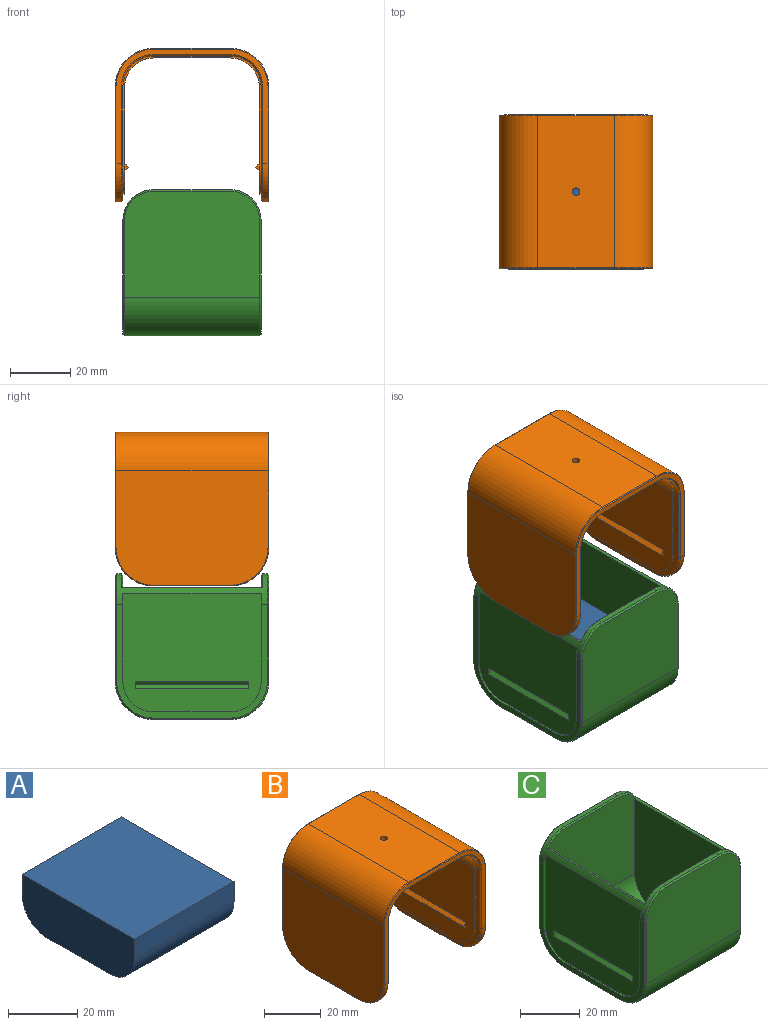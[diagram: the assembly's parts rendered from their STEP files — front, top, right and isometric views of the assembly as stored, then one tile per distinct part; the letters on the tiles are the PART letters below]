
ASSEMBLY  parts=3 mates=1
PART A: 8 faces, bbox 40.6x45.7x17.3 mm
  f0: plane 40.64x7.1mm, normal (0,1,0), area 288.6mm2, adj f1,f5,f6,f7
  f1: plane 45.72x40.64mm, normal (0,0,1), area 1858.1mm2, adj f0,f2,f6,f7
  f2: plane 40.64x7.1mm, normal (0,-1,0), area 288.6mm2, adj f1,f3,f6,f7
  f3: cylinder r=10.16mm len=40.64mm, axis (-1,0,0), area 648.6mm2, adj f2,f4,f6,f7
  f4: plane 40.64x25.4mm, normal (0,0,-1), area 1032.3mm2, adj f3,f5,f6,f7
  f5: cylinder r=10.16mm len=40.64mm, axis (-1,0,0), area 648.6mm2, adj f0,f4,f6,f7
  f6: plane 45.72x17.26mm, normal (1,0,0), area 744.9mm2, adj f0,f1,f2,f3,f4,f5
  f7: plane 45.72x17.26mm, normal (-1,0,0), area 744.9mm2, adj f0,f1,f2,f3,f4,f5
PART B: 75 faces, bbox 50.8x50.8x50.8 mm
  f0: plane 25.4x2.03mm, normal (0,0,-1), area 51.6mm2, adj f2,f12,f22,f43
  f1: cylinder r=10.16mm len=10.16mm, axis (0,1,0), area 32.4mm2, adj f3,f13,f21,f54
  f2: cylinder r=10.16mm len=10.16mm, axis (0,1,0), area 32.4mm2, adj f0,f4,f22,f45
  f3: plane 49.78x37.59mm, normal (1,0,0), area 226.2mm2, adj f1,f12,f21,f22,f29,f30,f31,f44
  f4: plane 49.78x37.59mm, normal (-1,0,0), area 226.2mm2, adj f2,f14,f21,f22,f23,f24,f25,f47
  f5: plane 25.4x1.78mm, normal (0,0,-1), area 45.2mm2, adj f18,f20,f51,f66
  f6: plane 50.29x37.85mm, normal (1,0,0), area 1836.9mm2, adj f7,f62,f64,f66,f68,f70
  f7: cylinder r=12.7mm len=50.29mm, axis (0,1,0), area 1003.3mm2, adj f6,f8,f60,f72
  f8: plane 50.29x25.4mm, normal (0,0,1), area 1272.3mm2, adj f7,f9,f58,f73,f74
  f9: cylinder r=12.7mm len=50.29mm, axis (0,1,0), area 1003.3mm2, adj f8,f10,f59,f71
  f10: plane 50.29x37.85mm, normal (-1,0,0), area 1836.9mm2, adj f9,f61,f63,f65,f67,f69
  f11: plane 25.4x1.78mm, normal (0,0,-1), area 45.2mm2, adj f17,f19,f48,f65
  f12: cylinder r=10.16mm len=10.16mm, axis (0,1,0), area 32.4mm2, adj f0,f3,f22,f42
  f13: plane 25.4x2.03mm, normal (0,0,-1), area 51.6mm2, adj f1,f14,f21,f56
  f14: cylinder r=10.16mm len=10.16mm, axis (0,1,0), area 32.4mm2, adj f4,f13,f21,f57
  f15: plane 50.29x37.85mm, normal (0,-1,0), area 200mm2, adj f19,f20,f42,f43,f44,f45,f47,f58
  f16: plane 50.29x37.85mm, normal (0,1,0), area 200mm2, adj f17,f18,f52,f54,f55,f56,f57,f69
  f17: cylinder r=12.7mm len=12.7mm, axis (1,0,0), area 35.5mm2, adj f11,f16,f50,f67
  f18: cylinder r=12.7mm len=12.7mm, axis (1,0,0), area 35.5mm2, adj f5,f16,f53,f68
  f19: cylinder r=12.7mm len=12.7mm, axis (-1,0,0), area 35.5mm2, adj f11,f15,f46,f63
  f20: cylinder r=12.7mm len=12.7mm, axis (-1,0,0), area 35.5mm2, adj f5,f15,f49,f64
  f21: plane 45.72x35.56mm, normal (0,1,0), area 68mm2, adj f1,f3,f4,f13,f14,f25,f26,f31
  f22: plane 45.72x35.56mm, normal (0,-1,0), area 68mm2, adj f0,f2,f3,f4,f12,f23,f26,f29
  f23: cylinder r=10.16mm len=10.16mm, axis (1,0,0), area 10.1mm2, adj f4,f22,f24,f26
  f24: plane 25.4x0.64mm, normal (0,0,-1), area 16.1mm2, adj f4,f23,f25,f26
  f25: cylinder r=10.16mm len=10.16mm, axis (1,0,0), area 10.1mm2, adj f4,f21,f24,f26
  f26: plane 45.72x35.56mm, normal (-1,0,0), area 1489.5mm2, adj f21,f22,f23,f24,f25,f27,f28,f35
  f27: plane 2.46x1.23mm, normal (0,-1,0), area 1.5mm2, adj f26,f35,f36
  f28: plane 2.46x1.23mm, normal (0,1,0), area 1.5mm2, adj f26,f35,f36
  f29: cylinder r=10.16mm len=10.16mm, axis (-1,0,0), area 10.1mm2, adj f3,f22,f30,f32
  f30: plane 25.4x0.64mm, normal (0,0,-1), area 16.1mm2, adj f3,f29,f31,f32
  f31: cylinder r=10.16mm len=10.16mm, axis (-1,0,0), area 10.1mm2, adj f3,f21,f30,f32
  f32: plane 45.72x35.56mm, normal (1,0,0), area 1489.5mm2, adj f21,f22,f29,f30,f31,f33,f34,f37
  f33: plane 2.46x1.23mm, normal (0,1,0), area 1.5mm2, adj f32,f37,f38
  f34: plane 2.46x1.23mm, normal (0,-1,0), area 1.5mm2, adj f32,f37,f38
  f35: plane 37.4x1.23mm, normal (-0.71,0,0.71), area 65.1mm2, adj f26,f27,f28,f36
  f36: plane 37.4x1.23mm, normal (-0.71,0,-0.71), area 65.1mm2, adj f26,f27,f28,f35
  f37: plane 37.4x1.23mm, normal (0.71,0,0.71), area 65.1mm2, adj f32,f33,f34,f38
  f38: plane 37.4x1.23mm, normal (0.71,0,-0.71), area 65.1mm2, adj f32,f33,f34,f37
  f39: cylinder r=9.53mm len=45.72mm, axis (0,-1,0), area 684.1mm2, adj f21,f22,f26,f41
  f40: cylinder r=9.53mm len=45.72mm, axis (0,-1,0), area 684.1mm2, adj f21,f22,f32,f41
  f41: plane 45.72x25.4mm, normal (0,0,-1), area 1156.2mm2, adj f21,f22,f39,f40,f74
  f42: cone r=10.67mm half-angle=45deg, axis (0,-1,0), area 11.8mm2, adj f12,f15,f43,f44
  f43: plane 25.4x0.51mm, normal (0,-0.71,-0.71), area 18.2mm2, adj f0,f15,f42,f45
  f44: plane 25.4x0.51mm, normal (0.71,-0.71,0), area 18.2mm2, adj f3,f15,f42,f46
  f45: cone r=10.16mm half-angle=45deg, axis (0,-1,0), area 11.8mm2, adj f2,f15,f43,f47
  f46: cone r=12.19mm half-angle=45deg, axis (-1,0,0), area 14mm2, adj f3,f19,f44,f48
  f47: plane 25.4x0.51mm, normal (-0.71,-0.71,0), area 18.2mm2, adj f4,f15,f45,f49
  f48: plane 25.4x0.51mm, normal (0.71,0,-0.71), area 18.2mm2, adj f3,f11,f46,f50
  f49: cone r=12.19mm half-angle=45deg, axis (1,0,0), area 14mm2, adj f4,f20,f47,f51
  f50: cone r=12.19mm half-angle=45deg, axis (-1,0,0), area 14mm2, adj f3,f17,f48,f52
  f51: plane 25.4x0.51mm, normal (-0.71,0,-0.71), area 18.2mm2, adj f4,f5,f49,f53
  f52: plane 25.4x0.51mm, normal (0.71,0.71,0), area 18.2mm2, adj f3,f16,f50,f54
  f53: cone r=12.19mm half-angle=45deg, axis (1,0,0), area 14mm2, adj f4,f18,f51,f55
  f54: cone r=10.16mm half-angle=45deg, axis (0,1,0), area 11.8mm2, adj f1,f16,f52,f56
  f55: plane 25.4x0.51mm, normal (-0.71,0.71,0), area 18.2mm2, adj f4,f16,f53,f57
  f56: plane 25.4x0.51mm, normal (0,0.71,-0.71), area 18.2mm2, adj f13,f16,f54,f57
  f57: cone r=10.67mm half-angle=45deg, axis (0,1,0), area 11.8mm2, adj f14,f16,f55,f56
  f58: plane 25.4x0.25mm, normal (0,-0.71,0.71), area 9.1mm2, adj f8,f15,f59,f60
  f59: cone r=12.7mm half-angle=45deg, axis (0,1,0), area 7.1mm2, adj f9,f15,f58,f61
  f60: cone r=12.45mm half-angle=45deg, axis (0,1,0), area 7.1mm2, adj f7,f15,f58,f62
  f61: plane 25.4x0.25mm, normal (-0.71,-0.71,0), area 9.1mm2, adj f10,f15,f59,f63
  f62: plane 25.4x0.25mm, normal (0.71,-0.71,0), area 9.1mm2, adj f6,f15,f60,f64
  f63: cone r=12.45mm half-angle=45deg, axis (1,0,0), area 7.1mm2, adj f10,f19,f61,f65
  f64: cone r=12.45mm half-angle=45deg, axis (-1,0,0), area 7.1mm2, adj f6,f20,f62,f66
  f65: plane 25.4x0.25mm, normal (-0.71,0,-0.71), area 9.1mm2, adj f10,f11,f63,f67
  f66: plane 25.4x0.25mm, normal (0.71,0,-0.71), area 9.1mm2, adj f5,f6,f64,f68
  f67: cone r=12.45mm half-angle=45deg, axis (1,0,0), area 7.1mm2, adj f10,f17,f65,f69
  f68: cone r=12.45mm half-angle=45deg, axis (-1,0,0), area 7.1mm2, adj f6,f18,f66,f70
  f69: plane 25.4x0.25mm, normal (-0.71,0.71,0), area 9.1mm2, adj f10,f16,f67,f71
  f70: plane 25.4x0.25mm, normal (0.71,0.71,0), area 9.1mm2, adj f6,f16,f68,f72
  f71: cone r=12.45mm half-angle=45deg, axis (0,-1,0), area 7.1mm2, adj f9,f16,f69,f73
  f72: cone r=12.7mm half-angle=45deg, axis (0,-1,0), area 7.1mm2, adj f7,f16,f70,f73
  f73: plane 25.4x0.25mm, normal (0,0.71,0.71), area 9.1mm2, adj f8,f16,f71,f72
  f74: cylinder r=1.27mm len=3.18mm, axis (0,0,1), area 25.3mm2, adj f8,f41
PART C: 62 faces, bbox 45.7x50.8x48.3 mm
  f0: plane 28.94x0.64mm, normal (0,1,0), area 17.6mm2, adj f5,f8,f28,f31
  f1: plane 41.44x35.08mm, normal (0,-1,0), area 1408.8mm2, adj f18,f19,f20,f54,f55,f56,f57,f59
  f2: plane 41.44x35.08mm, normal (0,1,0), area 1408.8mm2, adj f18,f19,f21,f56,f58,f59,f60,f61
  f3: plane 28.94x0.64mm, normal (0,-1,0), area 17.6mm2, adj f4,f10,f23,f25
  f4: plane 49.78x37.59mm, normal (-1,0,0), area 226.2mm2, adj f3,f10,f13,f22,f23,f24,f41,f43
  f5: plane 49.78x37.59mm, normal (1,0,0), area 226.2mm2, adj f0,f8,f14,f28,f29,f30,f42,f44
  f6: plane 25.4x1.55mm, normal (0,0,1), area 39.4mm2, adj f8,f10,f53,f55
  f7: plane 44.7x25.4mm, normal (0,0,-1), area 1135.5mm2, adj f15,f16,f45,f46
  f8: cylinder r=10.16mm len=49.78mm, axis (0,1,0), area 159.2mm2, adj f0,f5,f6,f9,f14,f31,f40,f52
  f9: plane 25.4x1.55mm, normal (0,0,1), area 39.4mm2, adj f8,f10,f38,f60
  f10: cylinder r=10.16mm len=49.78mm, axis (0,1,0), area 159.2mm2, adj f3,f4,f6,f9,f13,f25,f39,f51
  f11: plane 44.7x35.05mm, normal (0,-1,0), area 1527mm2, adj f16,f38,f39,f40,f41,f42
  f12: plane 44.7x35.05mm, normal (0,1,0), area 1527mm2, adj f15,f49,f50,f51,f52,f53
  f13: plane 28.94x0.64mm, normal (0,1,0), area 17.6mm2, adj f4,f10,f22,f25
  f14: plane 28.94x0.64mm, normal (0,-1,0), area 17.6mm2, adj f5,f8,f30,f31
  f15: cylinder r=12.7mm len=44.7mm, axis (1,0,0), area 891.8mm2, adj f7,f12,f47,f48
  f16: cylinder r=12.7mm len=44.7mm, axis (-1,0,0), area 891.8mm2, adj f7,f11,f43,f44
  f17: plane 40.64x25.4mm, normal (0,0,1), area 1032.3mm2, adj f18,f19,f20,f21
  f18: plane 45.72x40.86mm, normal (-1,0,0), area 1823.8mm2, adj f1,f2,f17,f20,f21,f56
  f19: plane 45.72x40.86mm, normal (1,0,0), area 1823.8mm2, adj f1,f2,f17,f20,f21,f59
  f20: cylinder r=10.16mm len=40.64mm, axis (1,0,0), area 648.6mm2, adj f1,f17,f18,f19
  f21: cylinder r=10.16mm len=40.64mm, axis (-1,0,0), area 648.6mm2, adj f2,f17,f18,f19
  f22: cylinder r=10.16mm len=10.16mm, axis (-1,0,0), area 10.1mm2, adj f4,f13,f24,f25
  f23: cylinder r=10.16mm len=10.16mm, axis (-1,0,0), area 10.1mm2, adj f3,f4,f24,f25
  f24: plane 25.4x0.64mm, normal (0,0,1), area 16.1mm2, adj f4,f22,f23,f25
  f25: plane 45.72x39.1mm, normal (-1,0,0), area 1651.1mm2, adj f3,f10,f13,f22,f23,f24,f26,f27
  f26: plane 2.46x1.23mm, normal (0,-1,0), area 1.5mm2, adj f25,f34,f35
  f27: plane 2.46x1.23mm, normal (0,1,0), area 1.5mm2, adj f25,f34,f35
  f28: cylinder r=10.16mm len=10.16mm, axis (1,0,0), area 10.1mm2, adj f0,f5,f29,f31
  f29: plane 25.4x0.64mm, normal (0,0,1), area 16.1mm2, adj f5,f28,f30,f31
  f30: cylinder r=10.16mm len=10.16mm, axis (1,0,0), area 10.1mm2, adj f5,f14,f29,f31
  f31: plane 45.72x39.1mm, normal (1,0,0), area 1651.1mm2, adj f0,f8,f14,f28,f29,f30,f32,f33
  f32: plane 2.46x1.23mm, normal (0,1,0), area 1.5mm2, adj f31,f36,f37
  f33: plane 2.46x1.23mm, normal (0,-1,0), area 1.5mm2, adj f31,f36,f37
  f34: plane 37.4x1.23mm, normal (-0.71,0,0.71), area 65.1mm2, adj f25,f26,f27,f35
  f35: plane 37.4x1.23mm, normal (-0.71,0,-0.71), area 65.1mm2, adj f25,f26,f27,f34
  f36: plane 37.4x1.23mm, normal (0.71,0,0.71), area 65.1mm2, adj f31,f32,f33,f37
  f37: plane 37.4x1.23mm, normal (0.71,0,-0.71), area 65.1mm2, adj f31,f32,f33,f36
  f38: plane 25.4x0.51mm, normal (0,-0.71,0.71), area 18.2mm2, adj f9,f11,f39,f40
  f39: cone r=10.16mm half-angle=45deg, axis (0,1,0), area 11.2mm2, adj f10,f11,f38,f41
  f40: cone r=9.65mm half-angle=45deg, axis (0,1,0), area 11.2mm2, adj f8,f11,f38,f42
  f41: plane 25.4x0.51mm, normal (-0.71,-0.71,0), area 18.2mm2, adj f4,f11,f39,f43
  f42: plane 25.4x0.51mm, normal (0.71,-0.71,0), area 18.2mm2, adj f5,f11,f40,f44
  f43: cone r=12.19mm half-angle=45deg, axis (1,0,0), area 14mm2, adj f4,f16,f41,f45
  f44: cone r=12.19mm half-angle=45deg, axis (-1,0,0), area 14mm2, adj f5,f16,f42,f46
  f45: plane 25.4x0.51mm, normal (-0.71,0,-0.71), area 18.2mm2, adj f4,f7,f43,f47
  f46: plane 25.4x0.51mm, normal (0.71,0,-0.71), area 18.2mm2, adj f5,f7,f44,f48
  f47: cone r=12.19mm half-angle=45deg, axis (1,0,0), area 14mm2, adj f4,f15,f45,f49
  f48: cone r=12.19mm half-angle=45deg, axis (-1,0,0), area 14mm2, adj f5,f15,f46,f50
  f49: plane 25.4x0.51mm, normal (-0.71,0.71,0), area 18.2mm2, adj f4,f12,f47,f51
  f50: plane 25.4x0.51mm, normal (0.71,0.71,0), area 18.2mm2, adj f5,f12,f48,f52
  f51: cone r=9.65mm half-angle=45deg, axis (0,-1,0), area 11.2mm2, adj f10,f12,f49,f53
  f52: cone r=10.16mm half-angle=45deg, axis (0,-1,0), area 11.2mm2, adj f8,f12,f50,f53
  f53: plane 25.4x0.51mm, normal (0,0.71,0.71), area 18.2mm2, adj f6,f12,f51,f52
  f54: cone r=10.16mm half-angle=45deg, axis (0,1,0), area 6.6mm2, adj f1,f8,f55,f56
  f55: plane 25.4x0.48mm, normal (0,-0.71,0.71), area 17.2mm2, adj f1,f6,f54,f57
  f56: plane 46.68x0.89mm, normal (-0.29,0,0.96), area 42.3mm2, adj f1,f2,f8,f18,f54,f58
  f57: cone r=9.68mm half-angle=45deg, axis (0,1,0), area 6.6mm2, adj f1,f10,f55,f59
  f58: cone r=10.16mm half-angle=45deg, axis (0,-1,0), area 6.6mm2, adj f2,f8,f56,f60
  f59: plane 46.68x0.89mm, normal (0.29,0,0.96), area 42.3mm2, adj f1,f2,f10,f19,f57,f61
  f60: plane 25.4x0.48mm, normal (0,0.71,0.71), area 17.2mm2, adj f2,f9,f58,f61
  f61: cone r=9.68mm half-angle=45deg, axis (0,-1,0), area 6.6mm2, adj f2,f10,f59,f60
PLACE A at identity
PLACE B t=(0,0,44.2)mm
PLACE C at identity
MATE fastened A.f4 <-> C.f17  axis (0,0,-1) through (0,-25.4,-22.86)mm
